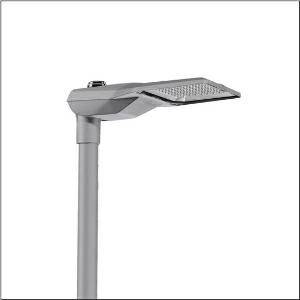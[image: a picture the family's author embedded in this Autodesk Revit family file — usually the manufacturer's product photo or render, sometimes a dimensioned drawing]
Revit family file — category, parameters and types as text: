
# Revit family: streetlight_sl_21_midi___st1_0a_5xe7d27n08nb_1197
name_source: partatom
category: Lighting Fixtures
units: mm (PartAtom-declared; Revit-internal decimal feet)

## family parameters
Cut with Voids When Loaded = No
Host = Face
Light Source = No
Part Type = Normal
Room Calculation Point = No
Round Connector Dimension = Use Diameter
Shared = No

## types (1)
- --- (1 x LED, 18780 lm, 151.2 W, 2200K)
    Apparent Load = 151 VA
    CIE Flux Codes = 40 73 97 100 100
    Color Rendering = 70
    Color Temperature = 2200K
    Default Elevation = 1800 mm
    Description = Streetlight SL 21 midi, mast luminaire, primary light control with lens, of PMMA, primary optical cover: cover, of toughened safety glass, transparent, light distribution: ST1.0a, light emission: direct distribution, primary light characteristic: asymmetric, installation type: side-entry, LED, 3G 2.5mm², High Power LED, rated luminous flux: 18.780lm, luminous efficacy: 124lm/W, light colour: 722, colour temperature: 2200K, control gear: NEMA (7pin), control: overheat protection, pre-setting: linear dimming characteristic, constant luminous flux control, time-dependent luminous flux control, flexible luminous flux parameterisation, mains connection: 220..240V, AC, 50/60Hz, connection cable pre-assembled, cable length: 12,5m, wiring characteristics: H05VV-F, start of lifetime: 151W, end of service life: 157W, reduction: 70W, luminaire housing, of diecast aluminium (EN AC-44300), powder-coated, Siteco® metallic grey (DB 702S), corrosivity category C5 mid according to DIN EN ISO 12944, multi-level sealing system, sealing non-destructively replaceable, inclination adjustable: 0°, 5°, 10°, 15°, length: 644mm, width: 335mm, height: 110mm, spigot size: 42mm (side-entry), mounting height: 4..8m, protection rating (complete): IP66, insulation class (complete): insulation class I (protective earthing), certification: CE, ENEC, ENEC+, VDE, impact resistance: IK09, permissible operating ambient temperature for outdoor applications: -40..+50°C, standard-compliant lighting for roads and squares, packaging unit: 1 piece

Light Distribution: ST1.0a
    Height = 111 mm
    Lamp = 1 x LED
    Lamp Light Flux = 18780 lm
    Lamp Power = 151.2 W
    Lamp count = 1
    Length = 644 mm
    Luminous efficacy = 124 lm/W
    Manufacturer = Siteco
    ModVariant = No
    Model = 5XE7D27N08NB
    Number of Poles = 1
    OnlyDefault = Yes
    Power Factor = 1
    Product Name = Streetlight SL 21 midi | ST1.0a
    Product group = mast luminaire | pylon top
    ProductGroupID = 6100
    Protection Class = Protection class I
    Protection Degree = IP 66
    RLX_Detail_Level = 1
    RLX_Emergency_Light_Flux = 0 lm
    RLX_Emergency_Type = 0
    RLX_Emergency_Type_DB = No
    RlxData = <blob elided: 90805 chars, md5=d1daecdd>
    Socket = socket
    Standby Power = 0 W
    System Light Flux = 18781 lm
    System Power = 151 W
    Type Comments = factory setting: luminous flux: 100 % | dim-lin: 254 | 802 mA
    Type Image = l_1294377.jpg
    URL = http://relux.com
    VarID = @adj_130510
    Voltage = 0 V
    Weight = 0.00 kg
    Width = 336 mm

## geometry (parser evidence)
native form markers: Blend x4, Sweep x12
no freeform markers — native parametric forms only
